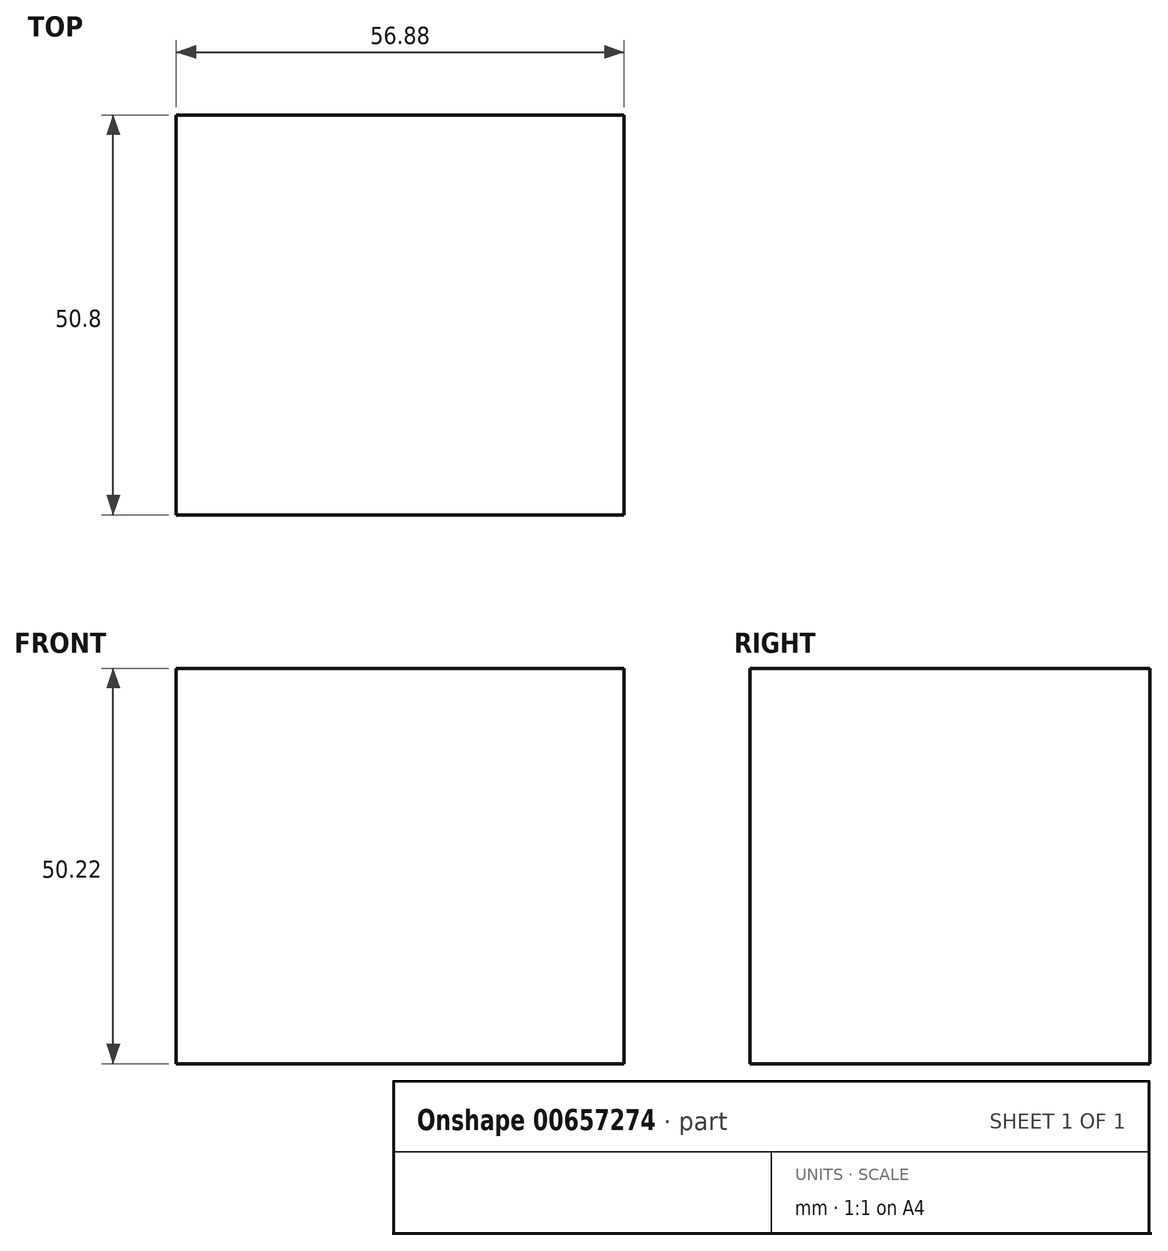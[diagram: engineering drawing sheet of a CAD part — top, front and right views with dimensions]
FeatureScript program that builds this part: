
annotation { "Feature Type Name" : "Feature", "Feature Type Description" : "" }
export const myFeature = defineFeature(function(context is Context, id is Id, definition is map)
    precondition{}
    {
        {
            var Q0;
            Q0=qCreatedBy(makeId("Front.planeOp"),FACE);
            var sketch = newSketch(context, id + "F0", { "sketchPlane" : qUnion([Q0])});
            skLineSegment(sketch, "E0.bottom", {"start": v(0, 0) * mm, "end": v(56.88, 0) * mm});
            skLineSegment(sketch, "E0.top", {"start": v(0, 50.22) * mm, "end": v(56.88, 50.22) * mm});
            skLineSegment(sketch, "E0.left", {"start": v(0, 0) * mm, "end": v(0, 50.22) * mm});
            skLineSegment(sketch, "E0.right", {"start": v(56.88, 0) * mm, "end": v(56.88, 50.22) * mm});
            skSolve(sketch);
        }
        {
            var Q0;
            Q0 = qSketchRegion(id + "F0", true);
            extrude(context, id + "F1", {"entities" : qUnion([Q0]), "depth" : 50.8 * mm, "offsetDistance" : 25.4 * mm});
        }
    });
